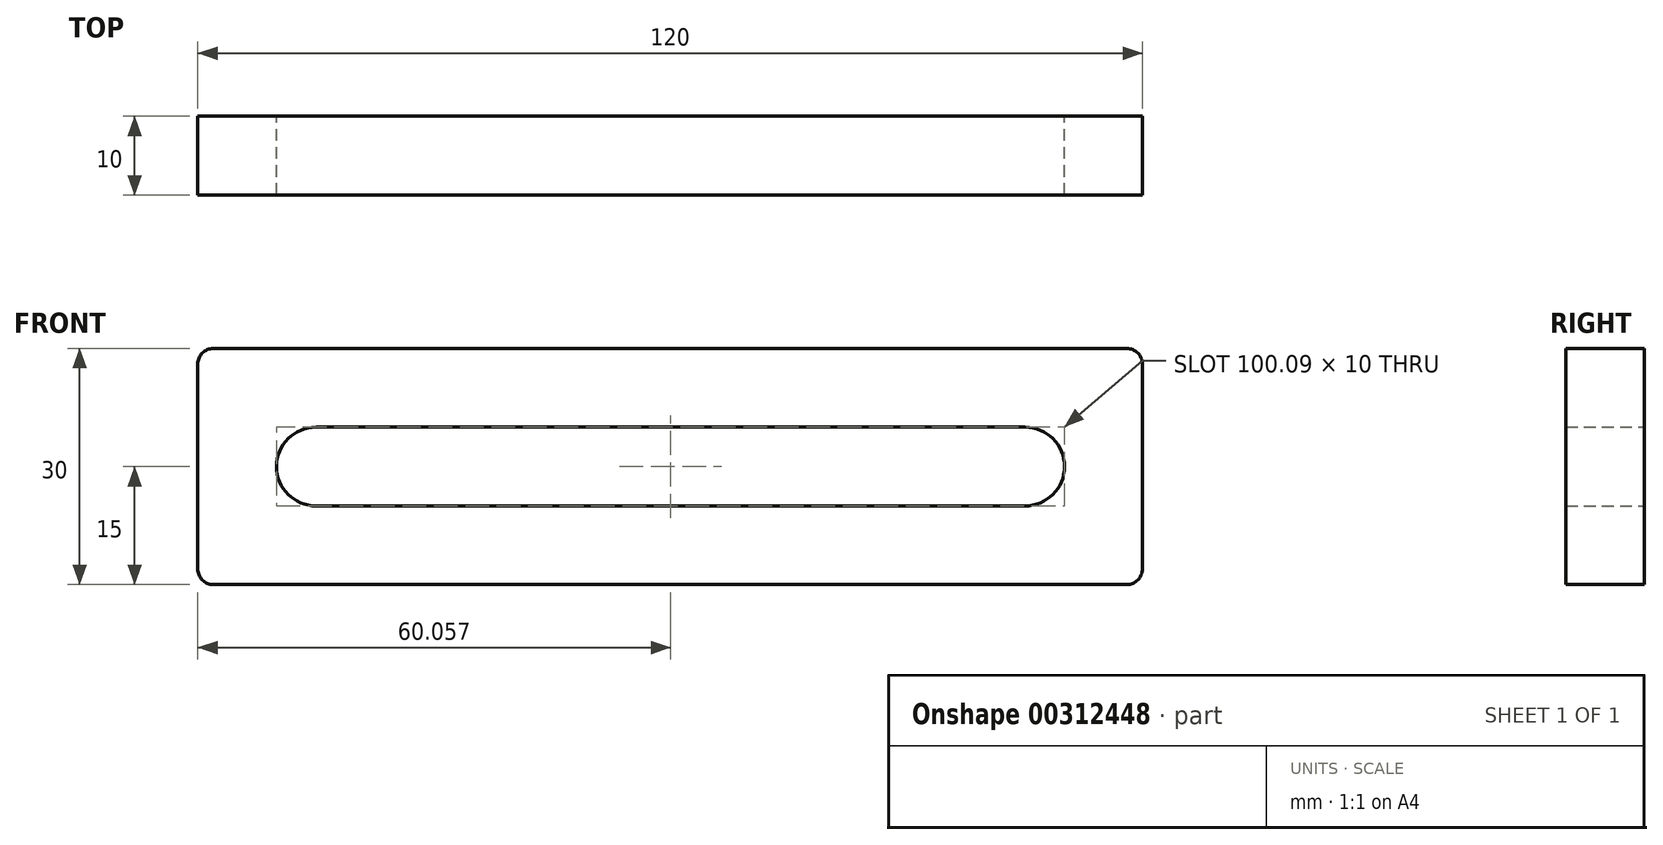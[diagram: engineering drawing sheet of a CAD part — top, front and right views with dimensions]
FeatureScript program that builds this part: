
annotation { "Feature Type Name" : "Feature", "Feature Type Description" : "" }
export const myFeature = defineFeature(function(context is Context, id is Id, definition is map)
    precondition{}
    {
        {
            var Q0;
            Q0=qCreatedBy(makeId("Front.planeOp"),FACE);
            var sketch = newSketch(context, id + "F0", { "sketchPlane" : qUnion([Q0])});
            skLineSegment(sketch, "E0.bottom", {"start": v(58, 15) * mm, "end": v(-58, 15) * mm});
            skLineSegment(sketch, "E0.top", {"start": v(58, -15) * mm, "end": v(-58, -15) * mm});
            skLineSegment(sketch, "E0.left", {"start": v(60, 13) * mm, "end": v(60, -13) * mm});
            skLineSegment(sketch, "E0.right", {"start": v(-60, 13) * mm, "end": v(-60, -13) * mm});
            skPoint(sketch, "E0.middle", {"position": v(0, 0) * mm});
            skLineSegment(sketch, "E1.bottom", {"start": v(45.1, 5) * mm, "end": v(-44.99, 5) * mm});
            skLineSegment(sketch, "E1.top", {"start": v(45.1, -5) * mm, "end": v(-44.99, -5) * mm});
            skLineSegment(sketch, "E1.left", {"start": v(50, 0.1) * mm, "end": v(50, 0) * mm});
            skPoint(sketch, "E2.middle", {"position": v(-44.99, 0) * mm});
            skArc(sketch, "E3", {"start": v(-44.99, 5) * mm, "mid": v(-49.99, 0) * mm, "end": v(-44.99, -5) * mm});
            skArc(sketch, "E4", {"start": v(45.1, -5) * mm, "mid": v(50.1, 0) * mm, "end": v(45.1, 5) * mm});
            skLineSegment(sketch, "E5", {"start": v(50.1, 0) * mm, "end": v(50, 0.1) * mm});
            skPoint(sketch, "E6.orphan", {"position": v(50, 5) * mm});
            skPoint(sketch, "E7.orphan", {"position": v(50, -5) * mm});
            skLineSegment(sketch, "E8.trimOffspring", {"start": v(50, 0) * mm, "end": v(50.1, 0) * mm});
            skPoint(sketch, "E9.orphan", {"position": v(-50, -5) * mm});
            skPoint(sketch, "E10.orphan", {"position": v(-50, 5) * mm});
            skPoint(sketch, "E11.orphan", {"position": v(-49.99, 0) * mm});
            skPoint(sketch, "E12.visualSharp", {"position": v(-60, 15) * mm});
            skArc(sketch, "E12.filletArc", {"start": v(-58, 15) * mm, "mid": v(-59.41, 14.41) * mm, "end": v(-60, 13) * mm});
            skPoint(sketch, "E13.visualSharp", {"position": v(-60, -15) * mm});
            skArc(sketch, "E13.filletArc", {"start": v(-60, -13) * mm, "mid": v(-59.41, -14.41) * mm, "end": v(-58, -15) * mm});
            skPoint(sketch, "E14.visualSharp", {"position": v(60, 15) * mm});
            skArc(sketch, "E14.filletArc", {"start": v(60, 13) * mm, "mid": v(59.41, 14.41) * mm, "end": v(58, 15) * mm});
            skPoint(sketch, "E15.visualSharp", {"position": v(60, -15) * mm});
            skArc(sketch, "E15.filletArc", {"start": v(58, -15) * mm, "mid": v(59.41, -14.41) * mm, "end": v(60, -13) * mm});
            skSolve(sketch);
        }
        {
            var Q0;
            Q0 = qSketchRegion(id + "F0", true);
            extrude(context, id + "F1", {"entities" : qUnion([Q0]), "depth" : 10 * mm});
        }
    });
